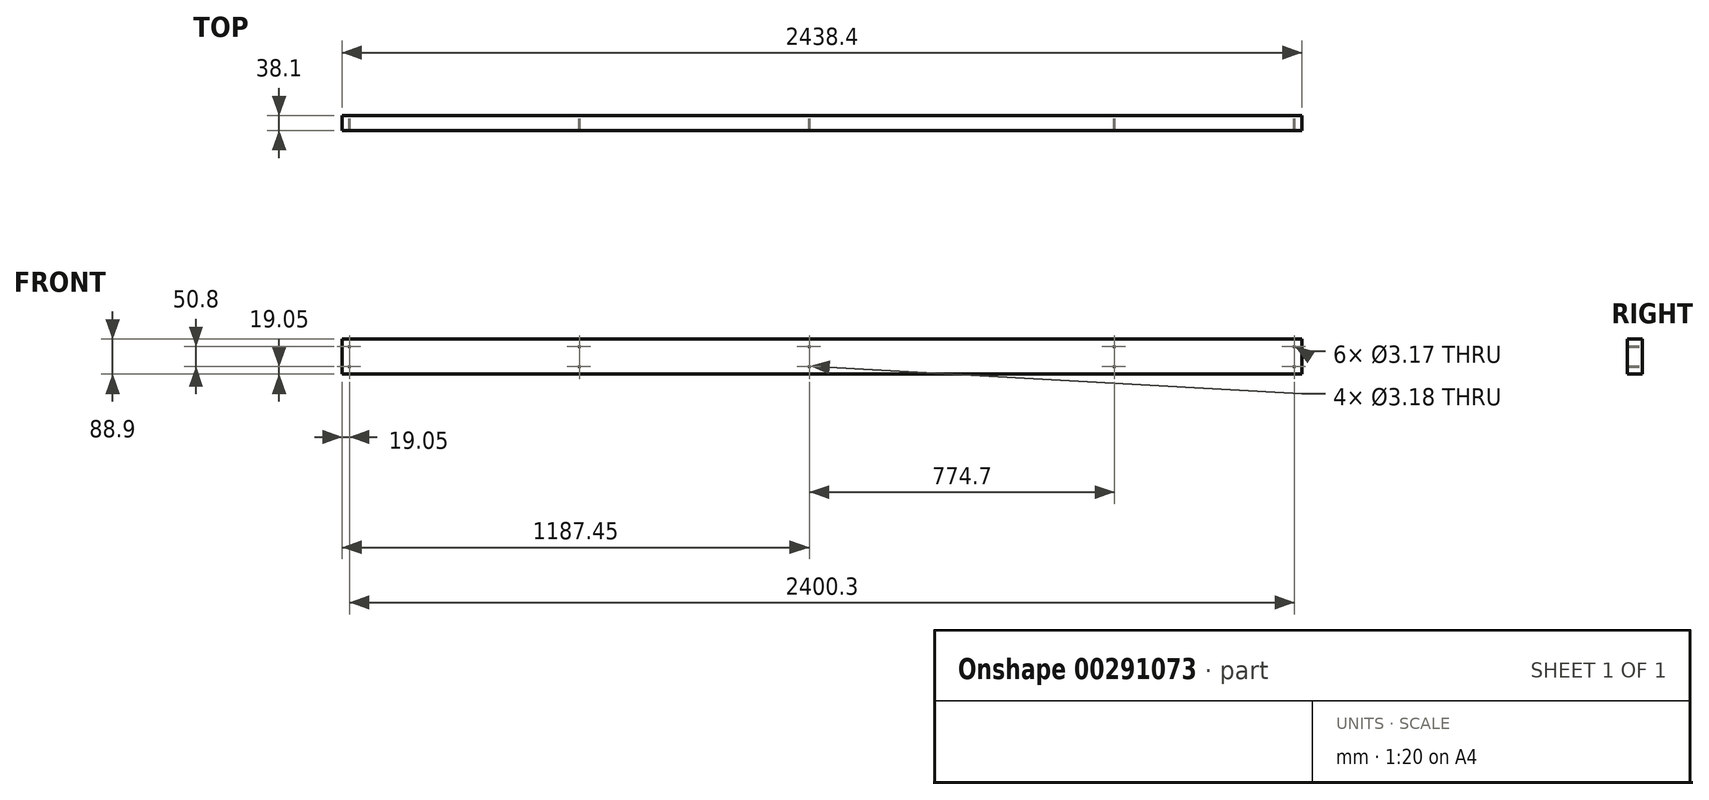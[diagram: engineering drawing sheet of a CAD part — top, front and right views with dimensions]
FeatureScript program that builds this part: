
annotation { "Feature Type Name" : "Feature", "Feature Type Description" : "" }
export const myFeature = defineFeature(function(context is Context, id is Id, definition is map)
    precondition{}
    {
        {
            var Q0;
            Q0=qCreatedBy(makeId("Front.planeOp"),FACE);
            var sketch = newSketch(context, id + "F0", { "sketchPlane" : qUnion([Q0])});
            skLineSegment(sketch, "E0.bottom", {"start": v(0, 0) * mm, "end": v(2438.4, 0) * mm});
            skLineSegment(sketch, "E0.top", {"start": v(0, -88.9) * mm, "end": v(2438.4, -88.9) * mm});
            skLineSegment(sketch, "E0.left", {"start": v(0, 0) * mm, "end": v(0, -88.9) * mm});
            skLineSegment(sketch, "E0.right", {"start": v(2438.4, 0) * mm, "end": v(2438.4, -88.9) * mm});
            skSolve(sketch);
        }
        {
            var Q0;
            Q0 = qSketchRegion(id + "F0", true);
            extrude(context, id + "F1", {"entities" : qUnion([Q0]), "depth" : 38.1 * mm});
        }
        {
            var Q0;
            Q0=qCreatedBy(makeId("Front.planeOp"),FACE);
            var sketch = newSketch(context, id + "F2", { "sketchPlane" : qUnion([Q0])});
            skCircle(sketch, "E1", {"center": v(19.05, -19.05) * mm, "radius": 1.59 * mm});
            skCircle(sketch, "E2.0.1.0", {"center": v(19.05, -69.85) * mm, "radius": 1.59 * mm});
            skCircle(sketch, "E2.1.0.0", {"center": v(2419.35, -19.05) * mm, "radius": 1.59 * mm});
            skCircle(sketch, "E2.1.1.0", {"center": v(2419.35, -69.85) * mm, "radius": 1.59 * mm});
            skCircle(sketch, "E2.2.0.0", {"center": v(4819.65, -19.05) * mm, "radius": 1.59 * mm});
            skCircle(sketch, "E2.2.1.0", {"center": v(4819.65, -69.85) * mm, "radius": 1.59 * mm});
            skLineSegment(sketch, "E2.direction1", {"start": v(19.05, -19.05) * mm, "end": v(2419.35, -19.05) * mm, "construction": true});
            skLineSegment(sketch, "E2.direction2", {"start": v(19.05, -69.85) * mm, "end": v(19.05, -19.05) * mm, "construction": true});
            skSolve(sketch);
        }
        {
            var Q0;
            Q0 = qSketchRegion(id + "F2", true);
            extrude(context, id + "F3", {"entities" : qUnion([Q0]), "operationType" : NewBodyOperationType.REMOVE, "endBound" : BoundingType.THROUGH_ALL, "depth" : 25.4 * mm});
        }
        {
            var Q0;
            Q0=qCreatedBy(makeId("Front.planeOp"),FACE);
            var sketch = newSketch(context, id + "F4", { "sketchPlane" : qUnion([Q0])});
            skCircle(sketch, "E3", {"center": v(1187.45, -19.05) * mm, "radius": 1.59 * mm});
            skCircle(sketch, "E4.0.1.0", {"center": v(1187.45, -69.85) * mm, "radius": 1.59 * mm});
            skCircle(sketch, "E4.1.0.0", {"center": v(1962.15, -19.05) * mm, "radius": 1.59 * mm});
            skCircle(sketch, "E4.1.1.0", {"center": v(1962.15, -69.85) * mm, "radius": 1.59 * mm});
            skLineSegment(sketch, "E4.direction1", {"start": v(1187.45, -19.05) * mm, "end": v(1962.15, -19.05) * mm, "construction": true});
            skLineSegment(sketch, "E4.direction2", {"start": v(1187.45, -19.05) * mm, "end": v(1187.45, -69.85) * mm, "construction": true});
            skSolve(sketch);
        }
        {
            var Q0;
            Q0 = qSketchRegion(id + "F4", true);
            extrude(context, id + "F5", {"entities" : qUnion([Q0]), "operationType" : NewBodyOperationType.REMOVE, "endBound" : BoundingType.THROUGH_ALL, "depth" : 25.4 * mm});
        }
        {
            var Q0;
            Q0=qCreatedBy(makeId("Front.planeOp"),FACE);
            var sketch = newSketch(context, id + "F6", { "sketchPlane" : qUnion([Q0])});
            skCircle(sketch, "E5", {"center": v(603.25, -19.05) * mm, "radius": 1.59 * mm});
            skCircle(sketch, "E6.0.1.0", {"center": v(603.25, -69.85) * mm, "radius": 1.59 * mm});
            skLineSegment(sketch, "E6.direction1", {"start": v(603.25, -19.05) * mm, "end": v(609.6, -19.05) * mm, "construction": true});
            skLineSegment(sketch, "E6.direction2", {"start": v(603.25, -19.05) * mm, "end": v(603.25, -69.85) * mm, "construction": true});
            skSolve(sketch);
        }
        {
            var Q0;
            Q0 = qSketchRegion(id + "F6", true);
            extrude(context, id + "F7", {"entities" : qUnion([Q0]), "operationType" : NewBodyOperationType.REMOVE, "endBound" : BoundingType.THROUGH_ALL, "depth" : 25.4 * mm});
        }
    });
